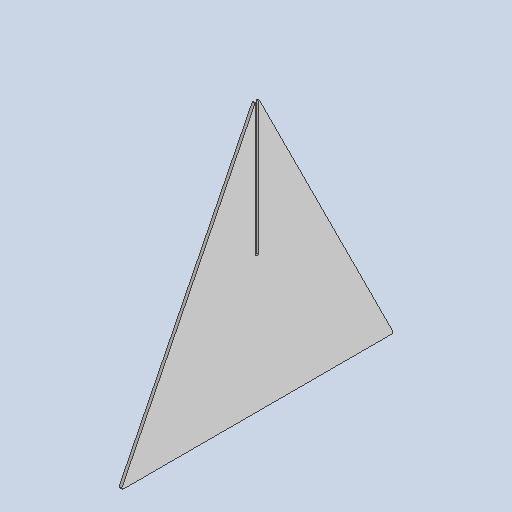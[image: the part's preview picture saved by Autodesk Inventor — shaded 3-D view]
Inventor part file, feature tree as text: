
AUTODESK INVENTOR PART (.ipt)
format: ipt  version: 2025 (Build 290162010, 162A)  size: 279,552 bytes
history: native  units: mm
features: other x3, sketch x2, sheet_metal_op x1, extrude x1
ambient origin geometry x8: Origin, YZ Plane, XZ Plane, XY Plane, X Axis, Y Axis, Z Axis, Center Point
bodies: Solid1 (feature_tree)
feature tree (7):
  sheet_metal_op  "Face1"
  extrude  "Extrusion1"  Depth=300.0mm
  other  "Corner Chamfer1"
  sketch  "Sketch1"  dims[d0=300.0mm d1=300.0mm]
  other  "Plate1"
  sketch  "Sketch2"  dims[d2=3.0mm d3=3.2mm d4=151.0mm d5=0.0mm d6=0.0mm d7=2.0mm d8=6.0mm d9=45.0deg]
  other  "Definition1"
